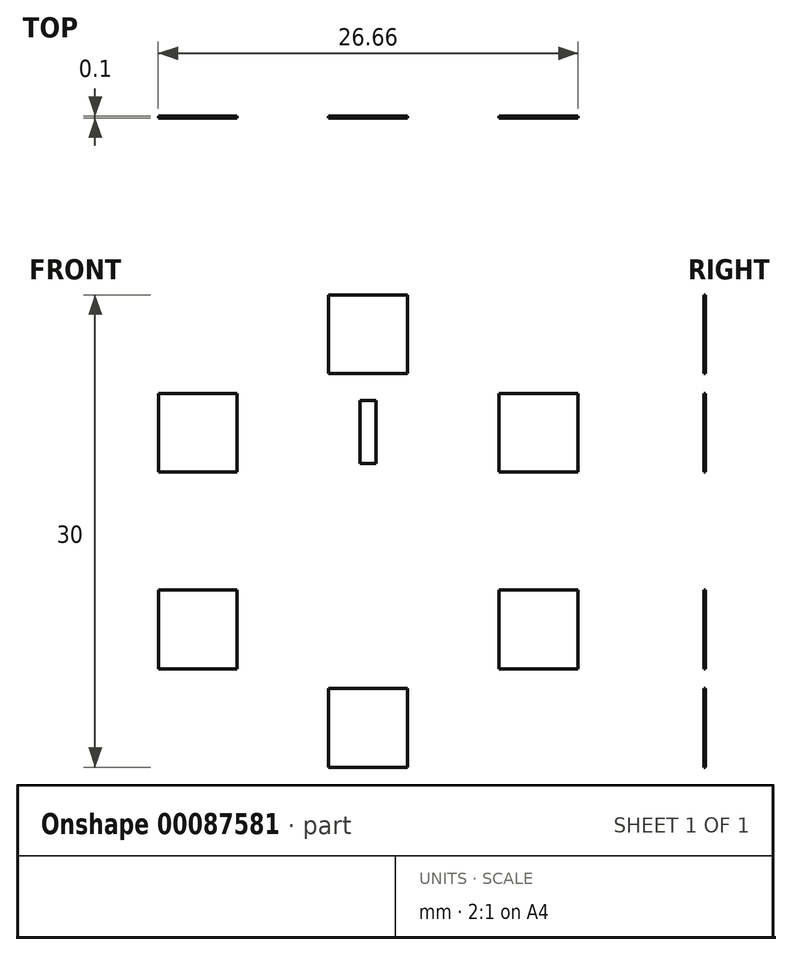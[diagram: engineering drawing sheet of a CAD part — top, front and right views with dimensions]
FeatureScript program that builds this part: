
annotation { "Feature Type Name" : "Feature", "Feature Type Description" : "" }
export const myFeature = defineFeature(function(context is Context, id is Id, definition is map)
    precondition{}
    {
        {
            var Q0;
            Q0=qCreatedBy(makeId("Front.planeOp"),FACE);
            var sketch = newSketch(context, id + "F0", { "sketchPlane" : qUnion([Q0])});
            skCircle(sketch, "E0", {"center": v(0, 0) * mm, "radius": 25.4 * mm, "construction": true});
            skCircle(sketch, "E1.cCircle", {"center": v(0, 0) * mm, "radius": 12.5 * mm, "construction": true});
            skLineSegment(sketch, "E1.0", {"start": v(0, 12.5) * mm, "end": v(10.83, 6.25) * mm, "construction": true});
            skLineSegment(sketch, "E1.1", {"start": v(10.83, 6.25) * mm, "end": v(10.83, -6.25) * mm, "construction": true});
            skLineSegment(sketch, "E1.2", {"start": v(10.83, -6.25) * mm, "end": v(0, -12.5) * mm, "construction": true});
            skLineSegment(sketch, "E1.3", {"start": v(0, -12.5) * mm, "end": v(-10.83, -6.25) * mm, "construction": true});
            skLineSegment(sketch, "E1.4", {"start": v(-10.83, -6.25) * mm, "end": v(-10.83, 6.25) * mm, "construction": true});
            skLineSegment(sketch, "E1.5", {"start": v(-10.83, 6.25) * mm, "end": v(0, 12.5) * mm, "construction": true});
            skLineSegment(sketch, "E2.bottom", {"start": v(2.5, 15) * mm, "end": v(-2.5, 15) * mm});
            skLineSegment(sketch, "E2.top", {"start": v(2.5, 10) * mm, "end": v(-2.5, 10) * mm});
            skLineSegment(sketch, "E2.left", {"start": v(2.5, 15) * mm, "end": v(2.5, 10) * mm});
            skLineSegment(sketch, "E2.right", {"start": v(-2.5, 15) * mm, "end": v(-2.5, 10) * mm});
            skPoint(sketch, "E2.middle", {"position": v(0, 12.5) * mm});
            skLineSegment(sketch, "E3.bottom", {"start": v(13.33, 8.75) * mm, "end": v(8.33, 8.75) * mm});
            skLineSegment(sketch, "E3.top", {"start": v(13.33, 3.75) * mm, "end": v(8.33, 3.75) * mm});
            skLineSegment(sketch, "E3.left", {"start": v(13.33, 8.75) * mm, "end": v(13.33, 3.75) * mm});
            skLineSegment(sketch, "E3.right", {"start": v(8.33, 8.75) * mm, "end": v(8.33, 3.75) * mm});
            skPoint(sketch, "E3.middle", {"position": v(10.83, 6.25) * mm});
            skLineSegment(sketch, "E4.bottom", {"start": v(13.33, -3.75) * mm, "end": v(8.33, -3.75) * mm});
            skLineSegment(sketch, "E4.top", {"start": v(13.33, -8.75) * mm, "end": v(8.33, -8.75) * mm});
            skLineSegment(sketch, "E4.left", {"start": v(13.33, -3.75) * mm, "end": v(13.33, -8.75) * mm});
            skLineSegment(sketch, "E4.right", {"start": v(8.33, -3.75) * mm, "end": v(8.33, -8.75) * mm});
            skPoint(sketch, "E4.middle", {"position": v(10.83, -6.25) * mm});
            skLineSegment(sketch, "E5.bottom", {"start": v(2.5, -15) * mm, "end": v(-2.5, -15) * mm});
            skLineSegment(sketch, "E5.top", {"start": v(2.5, -10) * mm, "end": v(-2.5, -10) * mm});
            skLineSegment(sketch, "E5.left", {"start": v(2.5, -15) * mm, "end": v(2.5, -10) * mm});
            skLineSegment(sketch, "E5.right", {"start": v(-2.5, -15) * mm, "end": v(-2.5, -10) * mm});
            skPoint(sketch, "E5.middle", {"position": v(0, -12.5) * mm});
            skLineSegment(sketch, "E6.bottom", {"start": v(-8.33, -3.75) * mm, "end": v(-13.33, -3.75) * mm});
            skLineSegment(sketch, "E6.top", {"start": v(-8.33, -8.75) * mm, "end": v(-13.33, -8.75) * mm});
            skLineSegment(sketch, "E6.left", {"start": v(-8.33, -3.75) * mm, "end": v(-8.33, -8.75) * mm});
            skLineSegment(sketch, "E6.right", {"start": v(-13.33, -3.75) * mm, "end": v(-13.33, -8.75) * mm});
            skPoint(sketch, "E6.middle", {"position": v(-10.83, -6.25) * mm});
            skLineSegment(sketch, "E7.bottom", {"start": v(-8.33, 3.75) * mm, "end": v(-13.33, 3.75) * mm});
            skLineSegment(sketch, "E7.top", {"start": v(-8.33, 8.75) * mm, "end": v(-13.33, 8.75) * mm});
            skLineSegment(sketch, "E7.left", {"start": v(-8.33, 3.75) * mm, "end": v(-8.33, 8.75) * mm});
            skLineSegment(sketch, "E7.right", {"start": v(-13.33, 3.75) * mm, "end": v(-13.33, 8.75) * mm});
            skPoint(sketch, "E7.middle", {"position": v(-10.83, 6.25) * mm});
            skLineSegment(sketch, "E8.bottom", {"start": v(0.5, 4.3) * mm, "end": v(-0.5, 4.3) * mm});
            skLineSegment(sketch, "E8.top", {"start": v(0.5, 8.3) * mm, "end": v(-0.5, 8.3) * mm});
            skLineSegment(sketch, "E8.left", {"start": v(0.5, 4.3) * mm, "end": v(0.5, 8.3) * mm});
            skLineSegment(sketch, "E8.right", {"start": v(-0.5, 4.3) * mm, "end": v(-0.5, 8.3) * mm});
            skPoint(sketch, "E8.middle", {"position": v(0, 6.3) * mm});
            skSolve(sketch);
        }
        {
            var Q0;
            Q0 = qSketchRegion(id + "F0", true);
            extrude(context, id + "F1", {"entities" : qUnion([Q0]), "depth" : .1 * mm});
        }
    });
